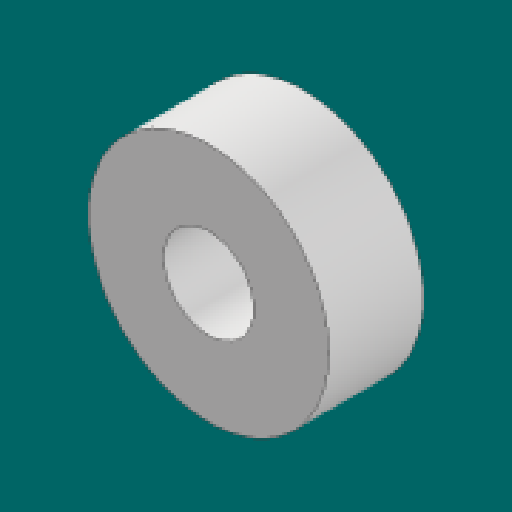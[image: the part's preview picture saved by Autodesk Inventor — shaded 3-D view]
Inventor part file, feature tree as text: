
AUTODESK INVENTOR PART (.ipt)
format: ipt  version: 2023.1 (Build 271208000, 208)  size: 93,184 bytes
history: native  units: in
note: dims shown in document units (in); Inventor stores cm internally (conversion verified against a paired STEP export)
features: extrude x1, sketch x1
ambient origin geometry x8: Origin, YZ Plane, XZ Plane, XY Plane, X Axis, Y Axis, Z Axis, Center Point
bodies: Solid1 (feature_tree)
feature tree (2):
  extrude  "Extrusion1"  Depth=0.196in
  sketch  "Sketch1"  dims[d0=0.1875in d1=0.5in d2=0.196in d3=0.0in]
